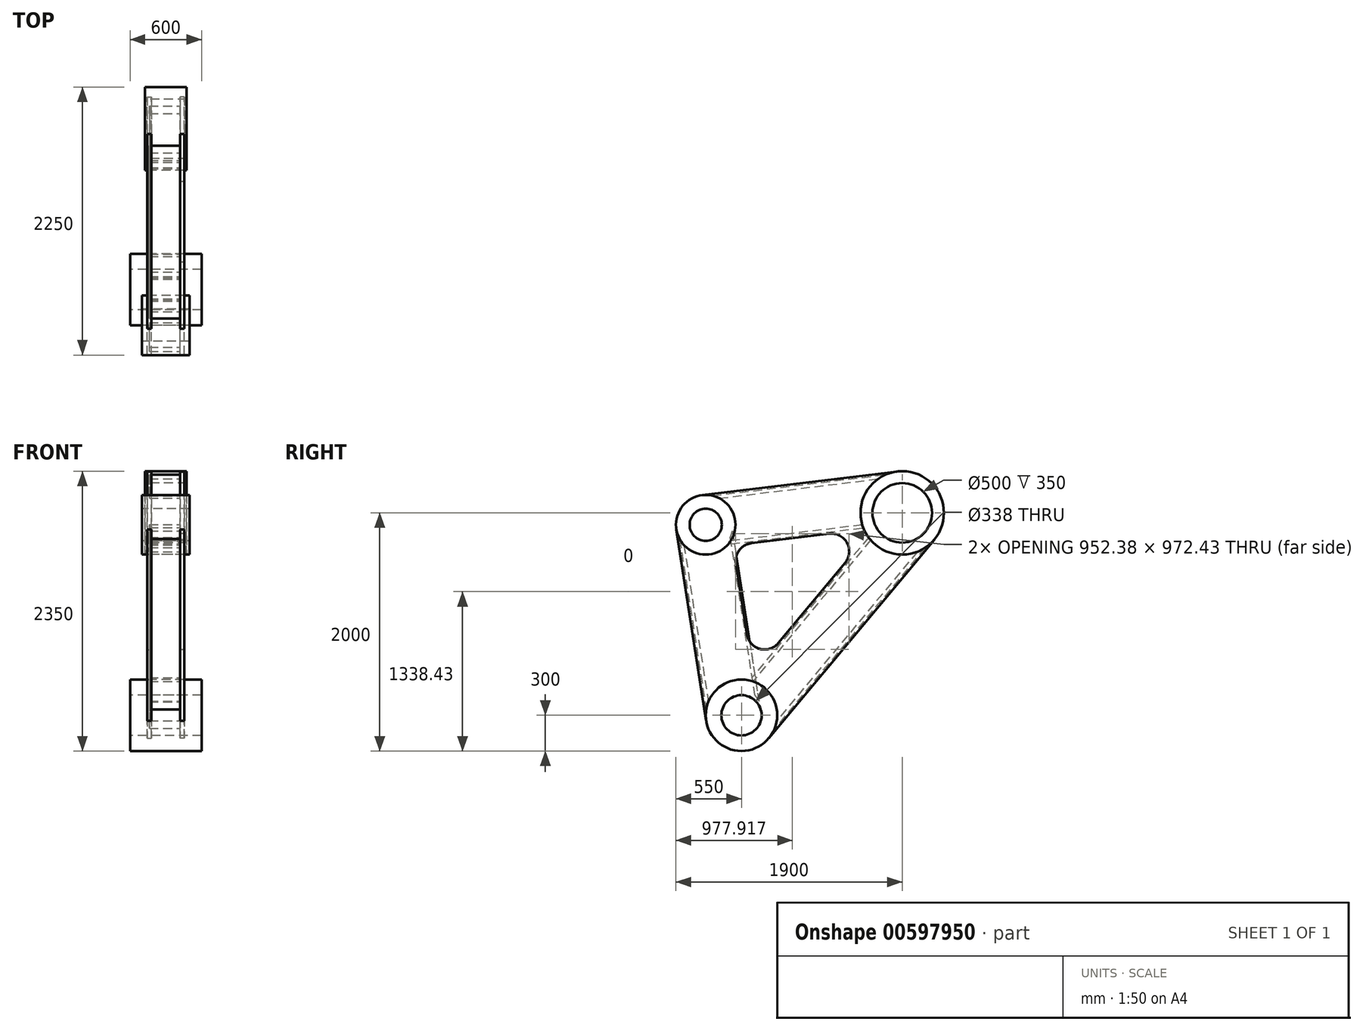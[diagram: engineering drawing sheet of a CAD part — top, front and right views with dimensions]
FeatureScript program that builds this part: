
annotation { "Feature Type Name" : "Feature", "Feature Type Description" : "" }
export const myFeature = defineFeature(function(context is Context, id is Id, definition is map)
    precondition{}
    {
        {
            var Q0;
            Q0=qCreatedBy(makeId("Right.planeOp"),FACE);
            var sketch = newSketch(context, id + "F0", { "sketchPlane" : qUnion([Q0])});
            skCircle(sketch, "E0", {"center": v(0, 0) * mm, "radius": 300 * mm});
            skCircle(sketch, "E1", {"center": v(0, 0) * mm, "radius": 169 * mm});
            skSolve(sketch);
        }
        {
            var Q0;
            Q0 = qSketchRegion(id + "F0", true);
            extrude(context, id + "F1", {"entities" : qUnion([Q0]), "endBound" : BoundingType.SYMMETRIC, "depth" : 600 * mm, "offsetDistance" : 25.4 * mm});
        }
        {
            var Q0;
            Q0=qCreatedBy(makeId("Right.planeOp"),FACE);
            var sketch = newSketch(context, id + "F2", { "sketchPlane" : qUnion([Q0])});
            skLineSegment(sketch, "E2", {"start": v(0, 0) * mm, "end": v(-300, 0) * mm, "construction": true});
            skLineSegment(sketch, "E3", {"start": v(-300, 0) * mm, "end": v(-300, 1600) * mm, "construction": true});
            skLineSegment(sketch, "E4", {"start": v(-300, 1600) * mm, "end": v(1350, 1600) * mm, "construction": true});
            skLineSegment(sketch, "E5", {"start": v(1350, 1600) * mm, "end": v(1350, 1700) * mm, "construction": true});
            skCircle(sketch, "E6", {"center": v(-300, 1600) * mm, "radius": 250 * mm});
            skCircle(sketch, "E7", {"center": v(-300, 1600) * mm, "radius": 135 * mm});
            skCircle(sketch, "E8", {"center": v(1350, 1700) * mm, "radius": 350 * mm});
            skCircle(sketch, "E9", {"center": v(1350, 1700) * mm, "radius": 250 * mm});
            skSolve(sketch);
        }
        {
            var Q0;
            Q0=makeQuery(id+"F2.imprint","IMPRINT",FACE,{"disambiguationData":[TD([[makeQuery(id+"F2.imprint","IMPRINT",EDGE,{"derivedFrom":sQuery(id+"F2.wireOp",EDGE,"E6")}),1.0]])]});
            extrude(context, id + "F3", {"entities" : qUnion([Q0]), "endBound" : BoundingType.SYMMETRIC, "depth" : 400 * mm, "offsetDistance" : 25 * mm});
        }
        {
            var Q0;
            Q0=makeQuery(id+"F2.imprint","IMPRINT",FACE,{"disambiguationData":[TD([[makeQuery(id+"F2.imprint","IMPRINT",EDGE,{"derivedFrom":sQuery(id+"F2.wireOp",EDGE,"E8")}),1.0]])]});
            extrude(context, id + "F4", {"entities" : qUnion([Q0]), "endBound" : BoundingType.SYMMETRIC, "depth" : 350 * mm, "offsetDistance" : 25 * mm});
        }
        {
            var Q0;
            Q0=qCreatedBy(makeId("Right.planeOp"),FACE);
            cPlane(context, id + "F5", {"entities" : qUnion([Q0]), "cplaneType" : CPlaneType.OFFSET, "offset" : 120 * mm, "width" : 150 * mm, "height" : 150 * mm});
        }
        {
            var Q0;
            Q0=qCreatedBy(id+"F5.planeOp",FACE);
            var sketch = newSketch(context, id + "F6", { "sketchPlane" : qUnion([Q0])});
            skArc(sketch, "E10.0", {"start": v(230.57, -191.93) * mm, "mid": v(79.95, 289.15) * mm, "end": v(-296.42, -46.2) * mm});
            skArc(sketch, "E11.0", {"start": v(-547.02, 1561.5) * mm, "mid": v(-100.6, 1449.2) * mm, "end": v(-330.2, 1848.17) * mm});
            skArc(sketch, "E12.0", {"start": v(1307.73, 2047.44) * mm, "mid": v(1042.65, 1532.56) * mm, "end": v(1619, 1476.09) * mm});
            skLineSegment(sketch, "E13", {"start": v(-330.2, 1848.17) * mm, "end": v(1307.73, 2047.44) * mm});
            skLineSegment(sketch, "E14", {"start": v(-547.02, 1561.5) * mm, "end": v(-296.42, -46.2) * mm});
            skLineSegment(sketch, "E15", {"start": v(1619, 1476.09) * mm, "end": v(230.57, -191.93) * mm});
            skLineSegment(sketch, "E16.0", {"start": v(870.1, 1279.78) * mm, "end": v(309.46, 606.24) * mm});
            skLineSegment(sketch, "E17.0", {"start": v(83.45, 1445.18) * mm, "end": v(736.7, 1524.65) * mm});
            skLineSegment(sketch, "E18.0", {"start": v(-46.64, 1273.17) * mm, "end": v(45.96, 679.1) * mm});
            skArc(sketch, "E19.filletArc", {"start": v(83.45, 1445.18) * mm, "mid": v(-18.07, 1386.76) * mm, "end": v(-46.64, 1273.17) * mm});
            skArc(sketch, "E20.filletArc", {"start": v(870.1, 1279.78) * mm, "mid": v(886.54, 1447.5) * mm, "end": v(736.7, 1524.65) * mm});
            skArc(sketch, "E21.filletArc", {"start": v(45.96, 679.1) * mm, "mid": v(154.2, 557.62) * mm, "end": v(309.46, 606.24) * mm});
            skSolve(sketch);
        }
        {
            var Q0;
            Q0 = qSketchRegion(id + "F6", true);
            extrude(context, id + "F7", {"entities" : qUnion([Q0]), "depth" : 35 * mm, "offsetDistance" : 25 * mm});
        }
        {
            var Q0;
            Q0=makeQuery(id+"F7.opExtrude","CAP_FACE",FACE,{"disambiguationData":[OSD([sQuery(id+"F6.wireOp",EDGE,"E10.0"),sQuery(id+"F6.wireOp",EDGE,"E11.0"),sQuery(id+"F6.wireOp",EDGE,"E12.0"),sQuery(id+"F6.wireOp",EDGE,"E13"),sQuery(id+"F6.wireOp",EDGE,"E14"),sQuery(id+"F6.wireOp",EDGE,"E15"),sQuery(id+"F6.wireOp",EDGE,"E16.0"),sQuery(id+"F6.wireOp",EDGE,"E17.0"),sQuery(id+"F6.wireOp",EDGE,"E18.0"),sQuery(id+"F6.wireOp",EDGE,"E19.filletArc"),sQuery(id+"F6.wireOp",EDGE,"E20.filletArc"),sQuery(id+"F6.wireOp",EDGE,"E21.filletArc")])],"isStart":true});
            var sketch = newSketch(context, id + "F8", { "sketchPlane" : qUnion([Q0])});
            skLineSegment(sketch, "E22.0", {"start": v(532.2, 1563.8) * mm, "end": v(281.6, -43.9) * mm});
            skLineSegment(sketch, "E23.0", {"start": v(504.53, 1568.12) * mm, "end": v(253.93, -39.58) * mm});
            skArc(sketch, "E24.0", {"start": v(-230.57, -191.93) * mm, "mid": v(-79.95, 289.15) * mm, "end": v(296.42, -46.2) * mm});
            skArc(sketch, "E25.0", {"start": v(547.02, 1561.5) * mm, "mid": v(100.6, 1449.2) * mm, "end": v(330.2, 1848.17) * mm});
            skLineSegment(sketch, "E26.0", {"start": v(328.38, 1833.28) * mm, "end": v(-1309.54, 2032.55) * mm});
            skLineSegment(sketch, "E27.0", {"start": v(325, 1805.48) * mm, "end": v(-1312.92, 2004.75) * mm});
            skArc(sketch, "E28.0", {"start": v(-1307.73, 2047.44) * mm, "mid": v(-1042.65, 1532.56) * mm, "end": v(-1619, 1476.09) * mm});
            skLineSegment(sketch, "E29.0", {"start": v(-1607.47, 1485.68) * mm, "end": v(-219.05, -182.33) * mm});
            skLineSegment(sketch, "E30.0", {"start": v(-1585.95, 1503.6) * mm, "end": v(-197.52, -164.42) * mm});
            skLineSegment(sketch, "E31.0", {"start": v(91.3, 1462.35) * mm, "end": v(-92.13, 285.5) * mm});
            skLineSegment(sketch, "E32.0", {"start": v(114.9, 1431.95) * mm, "end": v(-62.56, 293.4) * mm});
            skLineSegment(sketch, "E33.0", {"start": v(-1067.46, 1493.43) * mm, "end": v(-67.64, 292.28) * mm});
            skLineSegment(sketch, "E34.0", {"start": v(-1085.27, 1471.05) * mm, "end": v(-97.07, 283.86) * mm});
            skLineSegment(sketch, "E35.0", {"start": v(110.74, 1436.66) * mm, "end": v(-1023.23, 1574.62) * mm});
            skLineSegment(sketch, "E36.0", {"start": v(87.91, 1467.65) * mm, "end": v(-1014.08, 1601.71) * mm});
            skLineSegment(sketch, "E37", {"start": v(87.74, 1439.46) * mm, "end": v(114.9, 1431.95) * mm});
            skSolve(sketch);
        }
        {
            var Q0;
            {var subQ5=sQuery(id+"F8.wireOp",EDGE,"E34.0");Q0=makeQuery(id+"F8.imprint","IMPRINT",FACE,{"disambiguationData":[TD([[makeQuery(id+"F8.imprint","IMPRINT",EDGE,{"derivedFrom":subQ5}),1.0]])]});}
            var Q1;
            {var subQ0=sQuery(id+"F8.wireOp",EDGE,"E29.0");var subQ1=sQuery(id+"F8.wireOp",EDGE,"E24.0");var subQ2=makeQuery(id+"F8.imprint","INTERSECT",VERTEX,{"derivedFrom":[subQ1,subQ0]});Q1=makeQuery(id+"F8.imprint","IMPRINT",FACE,{"disambiguationData":[TD([[makeQuery(id+"F8.imprint","IMPRINT",EDGE,{"disambiguationData":[TD([[subQ2,-1.0]])],"derivedFrom":subQ1}),1.0]])]});}
            extrude(context, id + "F9", {"entities" : qUnion([Q0, Q1]), "depth" : 257 * mm, "offsetDistance" : 25 * mm});
        }
        {
            var Q0;
            {var subQ0=sQuery(id+"F8.wireOp",EDGE,"E27.0");var subQ1=sQuery(id+"F8.wireOp",EDGE,"E25.0");var subQ2=makeQuery(id+"F8.imprint","INTERSECT",VERTEX,{"derivedFrom":[subQ1,subQ0]});Q0=makeQuery(id+"F8.imprint","IMPRINT",FACE,{"disambiguationData":[TD([[makeQuery(id+"F8.imprint","IMPRINT",EDGE,{"disambiguationData":[TD([[subQ2,-1.0]])],"derivedFrom":subQ1}),1.0]])]});}
            var Q1;
            {var subQ7=sQuery(id+"F8.wireOp",EDGE,"E36.0");Q1=makeQuery(id+"F8.imprint","IMPRINT",FACE,{"disambiguationData":[TD([[makeQuery(id+"F8.imprint","IMPRINT",EDGE,{"derivedFrom":subQ7}),1.0]])]});}
            extrude(context, id + "F10", {"entities" : qUnion([Q0, Q1]), "depth" : 257 * mm, "offsetDistance" : 25 * mm});
        }
        {
            var Q0;
            {var subQ0=sQuery(id+"F8.wireOp",EDGE,"E24.0");var subQ1=sQuery(id+"F8.wireOp",EDGE,"E22.0");var subQ2=makeQuery(id+"F8.imprint","INTERSECT",VERTEX,{"derivedFrom":[subQ1,subQ0]});Q0=makeQuery(id+"F8.imprint","IMPRINT",FACE,{"disambiguationData":[TD([[makeQuery(id+"F8.imprint","IMPRINT",EDGE,{"disambiguationData":[TD([[subQ2,1.0]])],"derivedFrom":subQ1}),-1.0]])]});}
            extrude(context, id + "F11", {"entities" : qUnion([Q0]), "depth" : 257 * mm, "offsetDistance" : 25 * mm});
        }
        {
            var Q0;
            Q0=makeQuery(id+"F11.opExtrude","SWEPT_FACE",FACE,{"disambiguationData":[OSD([sQuery(id+"F8.wireOp",EDGE,"E23.0")])]});
            var Q1;
            Q1=makeQuery(id+"F10.opExtrude","SWEPT_FACE",FACE,{"disambiguationData":[OSD([sQuery(id+"F8.wireOp",EDGE,"E31.0")])]});
            cPlane(context, id + "F12", {"entities" : qUnion([Q0, Q1]), "cplaneType" : CPlaneType.MID_PLANE, "offset" : 25 * mm, "width" : 150 * mm, "height" : 150 * mm});
        }
        {
            var Q0;
            Q0=makeQuery(id+"F11.opExtrude","SWEPT_BODY",BODY,{"disambiguationData":[OSD([sQuery(id+"F8.wireOp",EDGE,"E22.0"),sQuery(id+"F8.wireOp",EDGE,"E23.0"),sQuery(id+"F8.wireOp",EDGE,"E24.0"),sQuery(id+"F8.wireOp",EDGE,"E25.0")])]});
            var Q1;
            Q1=qCreatedBy(id+"F12.planeOp",FACE);
            mirror(context, id + "F13", {"entities" : qUnion([Q0]), "mirrorPlane" : qUnion([Q1])});
        }
        {
            var Q0;
            Q0=makeQuery(id+"F7.opExtrude","SWEPT_BODY",BODY,{"disambiguationData":[OSD([sQuery(id+"F6.wireOp",EDGE,"E10.0"),sQuery(id+"F6.wireOp",EDGE,"E11.0"),sQuery(id+"F6.wireOp",EDGE,"E12.0"),sQuery(id+"F6.wireOp",EDGE,"E13"),sQuery(id+"F6.wireOp",EDGE,"E14"),sQuery(id+"F6.wireOp",EDGE,"E15"),sQuery(id+"F6.wireOp",EDGE,"E16.0"),sQuery(id+"F6.wireOp",EDGE,"E17.0"),sQuery(id+"F6.wireOp",EDGE,"E18.0"),sQuery(id+"F6.wireOp",EDGE,"E19.filletArc"),sQuery(id+"F6.wireOp",EDGE,"E20.filletArc"),sQuery(id+"F6.wireOp",EDGE,"E21.filletArc")])]});
            var Q1;
            Q1=qCreatedBy(makeId("Right.planeOp"),FACE);
            mirror(context, id + "F14", {"entities" : qUnion([Q0]), "mirrorPlane" : qUnion([Q1])});
        }
    });
